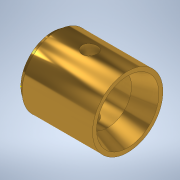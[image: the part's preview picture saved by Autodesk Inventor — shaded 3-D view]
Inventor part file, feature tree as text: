
AUTODESK INVENTOR PART (.ipt)
format: ipt  version: 2021 (Build 250183000, 183)  size: 162,816 bytes
history: native  units: mm
features: sketch x3, revolve x1, plane x1, hole x1
ambient origin geometry x8: Origin, YZ Plane, XZ Plane, XY Plane, X Axis, Y Axis, Z Axis, Center Point
bodies: Solid1 (feature_tree)
feature tree (6):
  revolve  "Revolution1"  [1 undecoded]
  sketch  "Sketch2"  dims[d5=4.75mm d6=6.2mm]
  plane  "Work Plane1"
  hole  "Hole1"  [1 undecoded]
  sketch  "Sketch1"  dims[d0=6.25mm d3=0.75mm]
  sketch  "Sketch3"  dims[d7=0.8mm d10=3.490659mm d11=11.0mm d12=90.0deg d13=7.0mm d14=7.5mm d15=3.0mm d16=3.0mm d17=6.0mm d18=4.0mm d19=2.0mm d20=90.0deg d21=8.0mm d22=20.594885mm]
note: 2 required parameter values undecoded (feature->parameter linkage not recoverable at this tier; creation-order binding heuristic only, values carry confidence <= 0.55)